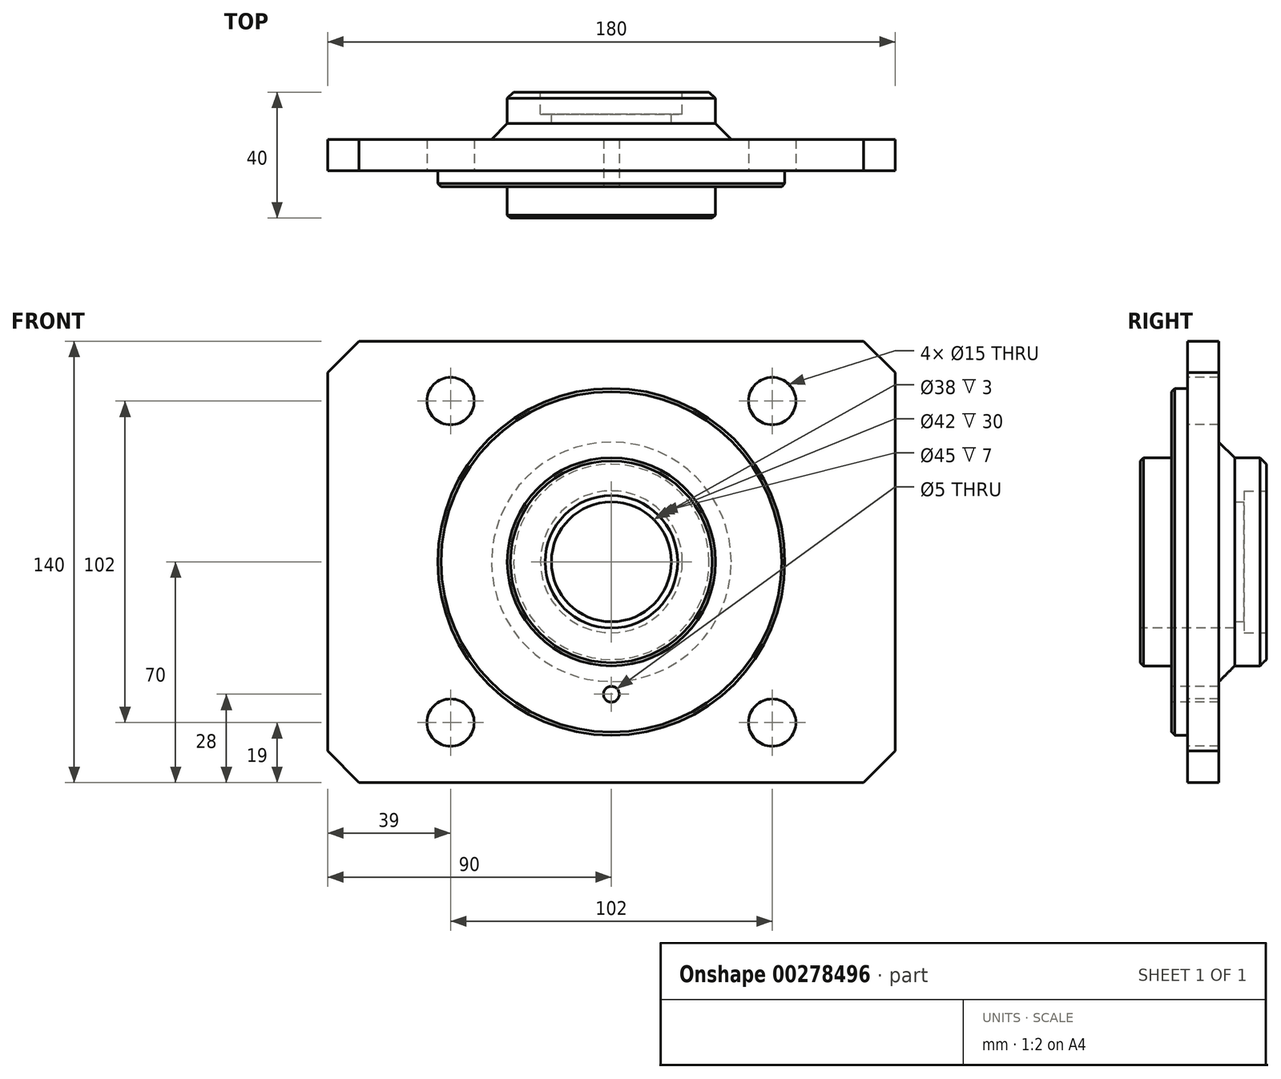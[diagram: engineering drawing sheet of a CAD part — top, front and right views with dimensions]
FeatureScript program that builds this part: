
annotation { "Feature Type Name" : "Feature", "Feature Type Description" : "" }
export const myFeature = defineFeature(function(context is Context, id is Id, definition is map)
    precondition{}
    {
        {
            var Q0;
            Q0=qCreatedBy(makeId("Front.planeOp"),FACE);
            var sketch = newSketch(context, id + "F0", { "sketchPlane" : qUnion([Q0])});
            skLineSegment(sketch, "E0.bottom", {"start": v(-90, -70) * mm, "end": v(90, -70) * mm});
            skLineSegment(sketch, "E0.top", {"start": v(-90, 70) * mm, "end": v(90, 70) * mm});
            skLineSegment(sketch, "E0.left", {"start": v(-90, -70) * mm, "end": v(-90, 70) * mm});
            skLineSegment(sketch, "E0.right", {"start": v(90, -70) * mm, "end": v(90, 70) * mm});
            skPoint(sketch, "E0.middle", {"position": v(0, 0) * mm});
            skCircle(sketch, "E1", {"center": v(0, 0) * mm, "radius": 55 * mm});
            skCircle(sketch, "E2", {"center": v(0, 0) * mm, "radius": 33 * mm});
            skCircle(sketch, "E3", {"center": v(0, 0) * mm, "radius": 19 * mm});
            skSolve(sketch);
        }
        {
            var Q0;
            Q0=makeQuery(id+"F0.imprint","IMPRINT",FACE,{"disambiguationData":[TD([[makeQuery(id+"F0.imprint","IMPRINT",EDGE,{"derivedFrom":sQuery(id+"F0.wireOp",EDGE,"E0.bottom")}),1.0]])]});
            extrude(context, id + "F1", {"entities" : qUnion([Q0]), "depth" : 10 * mm});
        }
        {
            var Q0;
            Q0=makeQuery(id+"F0.imprint","IMPRINT",FACE,{"disambiguationData":[TD([[makeQuery(id+"F0.imprint","IMPRINT",EDGE,{"derivedFrom":sQuery(id+"F0.wireOp",EDGE,"E1")}),1.0]])]});
            extrude(context, id + "F2", {"entities" : qUnion([Q0]), "operationType" : NewBodyOperationType.ADD, "depth" : 15 * mm});
        }
        {
            var Q0;
            Q0=makeQuery(id+"F0.imprint","IMPRINT",FACE,{"disambiguationData":[TD([[makeQuery(id+"F0.imprint","IMPRINT",EDGE,{"derivedFrom":sQuery(id+"F0.wireOp",EDGE,"E2")}),1.0]])]});
            extrude(context, id + "F3", {"entities" : qUnion([Q0]), "operationType" : NewBodyOperationType.ADD, "depth" : 25 * mm, "hasSecondDirection" : true, "secondDirectionOppositeDirection" : true, "secondDirectionDepth" : 15 * mm});
        }
        {
            var Q0;
            Q0=makeQuery(id+"F3.opExtrude","CAP_FACE",FACE,{"disambiguationData":[OSD([sQuery(id+"F0.wireOp",EDGE,"E2"),sQuery(id+"F0.wireOp",EDGE,"E3")])],"isStart":false});
            var sketch = newSketch(context, id + "F4", { "sketchPlane" : qUnion([Q0])});
            skCircle(sketch, "E4", {"center": v(0, 0) * mm, "radius": 21 * mm});
            skSolve(sketch);
        }
        {
            var Q0;
            Q0=makeQuery(id+"F4.imprint","IMPRINT",FACE,{"disambiguationData":[TD([[makeQuery(id+"F4.imprint","IMPRINT",EDGE,{"derivedFrom":sQuery(id+"F4.wireOp",EDGE,"E4")}),1.0]])]});
            extrude(context, id + "F5", {"entities" : qUnion([Q0]), "operationType" : NewBodyOperationType.REMOVE, "oppositeDirection" : true, "depth" : 30 * mm});
        }
        {
            var Q0;
            Q0=makeQuery(id+"F3.opExtrude","CAP_FACE",FACE,{"disambiguationData":[OSD([sQuery(id+"F0.wireOp",EDGE,"E2"),sQuery(id+"F0.wireOp",EDGE,"E3")])],"isStart":true});
            var sketch = newSketch(context, id + "F6", { "sketchPlane" : qUnion([Q0])});
            skCircle(sketch, "E5", {"center": v(0, 0) * mm, "radius": 22.5 * mm});
            skSolve(sketch);
        }
        {
            var Q0;
            Q0=makeQuery(id+"F6.imprint","IMPRINT",FACE,{"disambiguationData":[TD([[makeQuery(id+"F6.imprint","IMPRINT",EDGE,{"derivedFrom":sQuery(id+"F6.wireOp",EDGE,"E5")}),1.0]])]});
            extrude(context, id + "F7", {"entities" : qUnion([Q0]), "operationType" : NewBodyOperationType.REMOVE, "oppositeDirection" : true, "depth" : 7 * mm});
        }
        {
            var Q0;
            Q0=makeQuery(id+"F1.opExtrude","CAP_FACE",FACE,{"disambiguationData":[OSD([sQuery(id+"F0.wireOp",EDGE,"E0.bottom"),sQuery(id+"F0.wireOp",EDGE,"E0.top"),sQuery(id+"F0.wireOp",EDGE,"E0.left"),sQuery(id+"F0.wireOp",EDGE,"E0.right"),sQuery(id+"F0.wireOp",EDGE,"E1")])],"isStart":false});
            var sketch = newSketch(context, id + "F8", { "sketchPlane" : qUnion([Q0])});
            skLineSegment(sketch, "E6.bottom", {"start": v(-51, -51) * mm, "end": v(51, -51) * mm, "construction": true});
            skLineSegment(sketch, "E6.top", {"start": v(-51, 51) * mm, "end": v(51, 51) * mm, "construction": true});
            skLineSegment(sketch, "E6.left", {"start": v(-51, -51) * mm, "end": v(-51, 51) * mm, "construction": true});
            skLineSegment(sketch, "E6.right", {"start": v(51, -51) * mm, "end": v(51, 51) * mm, "construction": true});
            skPoint(sketch, "E6.middle", {"position": v(0, 0) * mm});
            skPoint(sketch, "E7", {"position": v(-51, 51) * mm});
            skPoint(sketch, "E8", {"position": v(51, 51) * mm});
            skPoint(sketch, "E9", {"position": v(51, -51) * mm});
            skPoint(sketch, "E10", {"position": v(-51, -51) * mm});
            skSolve(sketch);
        }
        {
            var Q0;
            Q0=sQuery(id+"F8.wireOp",VERTEX,"E7");
            var Q1;
            Q1=sQuery(id+"F8.wireOp",VERTEX,"E8");
            var Q2;
            Q2=sQuery(id+"F8.wireOp",VERTEX,"E9");
            var Q3;
            Q3=sQuery(id+"F8.wireOp",VERTEX,"E10");
            var Q4;
            Q4=makeQuery(id+"F1.opExtrude","SWEPT_BODY",BODY,{"disambiguationData":[OSD([sQuery(id+"F0.wireOp",EDGE,"E0.bottom"),sQuery(id+"F0.wireOp",EDGE,"E0.top"),sQuery(id+"F0.wireOp",EDGE,"E0.left"),sQuery(id+"F0.wireOp",EDGE,"E0.right"),sQuery(id+"F0.wireOp",EDGE,"E1")])]});
            hole(context, id + "F9", {"style" : HoleStyle.SIMPLE, "endStyle" : HoleEndStyle.THROUGH, "holeDiameter" : 15 * mm, "tappedDepth" : 12 * mm, "tapClearance" : 3, "locations" : qUnion([Q0, Q1, Q2, Q3]), "scope" : qUnion([Q4])});
        }
        {
            var Q0;
            Q0=makeQuery(id+"F2.opExtrude","CAP_FACE",FACE,{"disambiguationData":[OSD([sQuery(id+"F0.wireOp",EDGE,"E1"),sQuery(id+"F0.wireOp",EDGE,"E2")])],"isStart":false});
            var sketch = newSketch(context, id + "F10", { "sketchPlane" : qUnion([Q0])});
            skPoint(sketch, "E11", {"position": v(0, -42) * mm});
            skSolve(sketch);
        }
        {
            var Q0;
            Q0=sQuery(id+"F10.wireOp",VERTEX,"E11");
            var Q1;
            Q1=makeQuery(id+"F1.opExtrude","SWEPT_BODY",BODY,{"disambiguationData":[OSD([sQuery(id+"F0.wireOp",EDGE,"E0.bottom"),sQuery(id+"F0.wireOp",EDGE,"E0.top"),sQuery(id+"F0.wireOp",EDGE,"E0.left"),sQuery(id+"F0.wireOp",EDGE,"E0.right"),sQuery(id+"F0.wireOp",EDGE,"E1")])]});
            hole(context, id + "F11", {"style" : HoleStyle.SIMPLE, "endStyle" : HoleEndStyle.THROUGH, "holeDiameter" : 5 * mm, "tappedDepth" : 12 * mm, "tapClearance" : 3, "locations" : qUnion([Q0]), "scope" : qUnion([Q1])});
        }
        {
            var Q0;
            Q0=makeQuery(id+"F1.opExtrude","SWEPT_EDGE",EDGE,{"disambiguationData":[OSD([sQuery(id+"F0.wireOp",EDGE,"E0.top"),sQuery(id+"F0.wireOp",EDGE,"E0.left")])]});
            var Q1;
            Q1=makeQuery(id+"F1.opExtrude","SWEPT_EDGE",EDGE,{"disambiguationData":[OSD([sQuery(id+"F0.wireOp",EDGE,"E0.bottom"),sQuery(id+"F0.wireOp",EDGE,"E0.left")])]});
            var Q2;
            Q2=makeQuery(id+"F1.opExtrude","SWEPT_EDGE",EDGE,{"disambiguationData":[OSD([sQuery(id+"F0.wireOp",EDGE,"E0.top"),sQuery(id+"F0.wireOp",EDGE,"E0.right")])]});
            var Q3;
            Q3=makeQuery(id+"F1.opExtrude","SWEPT_EDGE",EDGE,{"disambiguationData":[OSD([sQuery(id+"F0.wireOp",EDGE,"E0.bottom"),sQuery(id+"F0.wireOp",EDGE,"E0.right")])]});
            chamfer(context, id + "F12", {"entities" : qUnion([Q0, Q1, Q2, Q3]), "chamferType" : ChamferType.OFFSET_ANGLE, "width" : 10 * mm, "oppositeDirection" : false, "angle" : 45 * degree, "tangentPropagation" : true});
        }
        {
            var Q0;
            Q0=makeQuery(id+"F2.opExtrude","CAP_EDGE",EDGE,{"disambiguationData":[OSD([sQuery(id+"F0.wireOp",EDGE,"E2")])],"isStart":true});
            chamfer(context, id + "F13", {"entities" : qUnion([Q0]), "chamferType" : ChamferType.OFFSET_ANGLE, "width" : 5 * mm, "oppositeDirection" : false, "angle" : 45 * degree, "tangentPropagation" : true});
        }
        {
            var Q0;
            Q0=makeQuery(id+"F3.opExtrude","CAP_EDGE",EDGE,{"disambiguationData":[OSD([sQuery(id+"F0.wireOp",EDGE,"E2")])],"isStart":true});
            chamfer(context, id + "F14", {"entities" : qUnion([Q0]), "chamferType" : ChamferType.OFFSET_ANGLE, "width" : 2 * mm, "oppositeDirection" : false, "angle" : 45 * degree, "tangentPropagation" : true});
        }
        {
            var Q0;
            Q0=makeQuery(id+"F7.boolean.opBoolean","COPY",EDGE,{"derivedFrom":makeQuery(id+"F7.opExtrude","CAP_EDGE",EDGE,{"disambiguationData":[OSD([sQuery(id+"F6.wireOp",EDGE,"E5")])],"isStart":true})});
            var Q1;
            Q1=makeQuery(id+"F5.boolean.opBoolean","COPY",EDGE,{"derivedFrom":makeQuery(id+"F5.opExtrude","CAP_EDGE",EDGE,{"disambiguationData":[OSD([sQuery(id+"F4.wireOp",EDGE,"E4")])],"isStart":true})});
            var Q2;
            Q2=makeQuery(id+"F3.opExtrude","CAP_EDGE",EDGE,{"disambiguationData":[OSD([sQuery(id+"F0.wireOp",EDGE,"E2")])],"isStart":false});
            var Q3;
            Q3=makeQuery(id+"F2.opExtrude","CAP_EDGE",EDGE,{"disambiguationData":[OSD([sQuery(id+"F0.wireOp",EDGE,"E1")])],"isStart":false});
            chamfer(context, id + "F15", {"entities" : qUnion([Q0, Q1, Q2, Q3]), "chamferType" : ChamferType.OFFSET_ANGLE, "width" : 1 * mm, "oppositeDirection" : false, "angle" : 45 * degree, "tangentPropagation" : true});
        }
    });
